# Revit family: Основная надпись. Форма 3
name_source: partatom
category: Основные надписи
units: mm (PartAtom-declared; Revit-internal decimal feet)

## family parameters
Повернуть с компонентом = Нет

## types (17) — shared parameters

## per-type parameters (varying)
| type | Высота | Дата выпуска проекта | Формат и кратность | Ширина |
| А2А | 420 мм | Нет | А2А | 594 мм |
| А3А | 297 мм | Нет | А3А | 420 мм |
| А1А | 594 мм | Нет | А1А | 841 мм |
| А1К | 840 мм | Нет | А1К | 594 мм |
| А0 | 841 мм | Нет | А0 | 1189 мм |
| А0 А | 841 мм | Да | А0А | 1189 мм |
| А0 К | 1189 мм | Нет | А0 | 841 мм |
| А3Х3 | 420 мм | Нет | А3Х3 | 891 мм |
| А2х3 | 594 мм | Нет | А2х3 | 1261 мм |
| А1А (1900х594 мм) | 594 мм | Нет | 1900х594мм (h) | 1900 мм |
| А1А (1000х594 мм) | 594 мм | Нет | 1000х594мм (h) | 1000 мм |
| А1А (1300х594 мм) | 594 мм | Нет | 1300х594мм (h) | 1300 мм |
| А1А (1680х594 мм) | 594 мм | Нет | 1680х594мм (h) | 1680 мм |
| А1А нормальный | 594 мм | Нет | А1А | 841 мм |
| А1А 594х1000 | 594 мм | Нет | А1А | 1000 мм |
| А0х2 А | 1189 мм | Нет | А0х2 | 1682 мм |
| А0х2 неизвестно | 1470 мм | Нет | А0 | 1189 мм |
